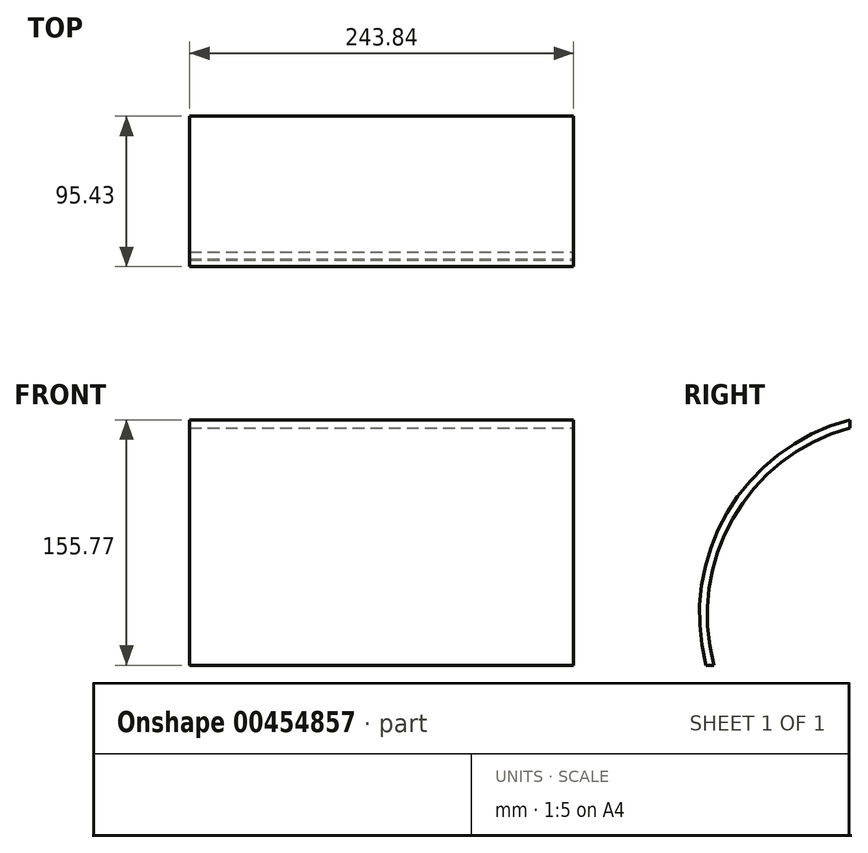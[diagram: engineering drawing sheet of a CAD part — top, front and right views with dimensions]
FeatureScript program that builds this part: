
annotation { "Feature Type Name" : "Feature", "Feature Type Description" : "" }
export const myFeature = defineFeature(function(context is Context, id is Id, definition is map)
    precondition{}
    {
        {
            var Q0;
            Q0=qCreatedBy(makeId("Front.planeOp"),FACE);
            var sketch = newSketch(context, id + "F0", { "sketchPlane" : qUnion([Q0])});
            skLineSegment(sketch, "E0.bottom", {"start": v(-121.92, 10.04) * mm, "end": v(121.92, 10.04) * mm});
            skLineSegment(sketch, "E0.top", {"start": v(-121.92, 4.96) * mm, "end": v(121.92, 4.96) * mm});
            skLineSegment(sketch, "E0.left", {"start": v(-121.92, 10.04) * mm, "end": v(-121.92, 4.96) * mm});
            skLineSegment(sketch, "E0.right", {"start": v(121.92, 10.04) * mm, "end": v(121.92, 4.96) * mm});
            skPoint(sketch, "E0.middle", {"position": v(0, 7.5) * mm});
            skSolve(sketch);
        }
        {
            var Q0;
            Q0=qCreatedBy(makeId("Right.planeOp"),FACE);
            var sketch = newSketch(context, id + "F1", { "sketchPlane" : qUnion([Q0])});
            skArc(sketch, "E1", {"start": v(0, 9.35) * mm, "mid": v(-77.42, -49.43) * mm, "end": v(-90.6, -145.73) * mm});
            skSolve(sketch);
        }
        {
            var Q0;
            Q0=makeQuery(id+"F0.imprint","IMPRINT",FACE,{"disambiguationData":[TD([[makeQuery(id+"F0.imprint","IMPRINT",EDGE,{"derivedFrom":sQuery(id+"F0.wireOp",EDGE,"E0.bottom")}),-1.0]])]});
            var Q1;
            Q1=sQuery(id+"F1.wireOp",EDGE,"E1");
            sweep(context, id + "F2", {"profiles" : qUnion([Q0]), "path" : qUnion([Q1])});
        }
    });
